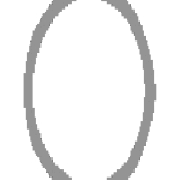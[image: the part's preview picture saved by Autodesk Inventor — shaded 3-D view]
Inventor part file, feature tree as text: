
AUTODESK INVENTOR PART (.ipt)
format: ipt  version: 2021 (Build 250183000, 183)  size: 112,640 bytes
history: native  units: in
note: dims shown in document units (in); Inventor stores cm internally (conversion verified against a paired STEP export)
features: other x4, sketch x3, plane x1
ambient origin geometry x8: Origin, YZ Plane, XZ Plane, XY Plane, X Axis, Y Axis, Z Axis, Center Point
bodies: Solid1 (feature_tree), Body (feature_tree)
feature tree (8):
  other  "Driven Length"
  other  "Frame Generator"
  other  "Start Plane"
  other  "End Plane"
  sketch  "Sketch"  dims[d2=20.0in d4=-0.0in d5=20.0in d6=0.12in d7=0.0in d8=90.0deg d9=20.0in]
  sketch  "Sketch2"  dims[d0=1.0in]
  plane  "Work Plane3"
  sketch  "Sketch3"  dims[d1=0.065in]
